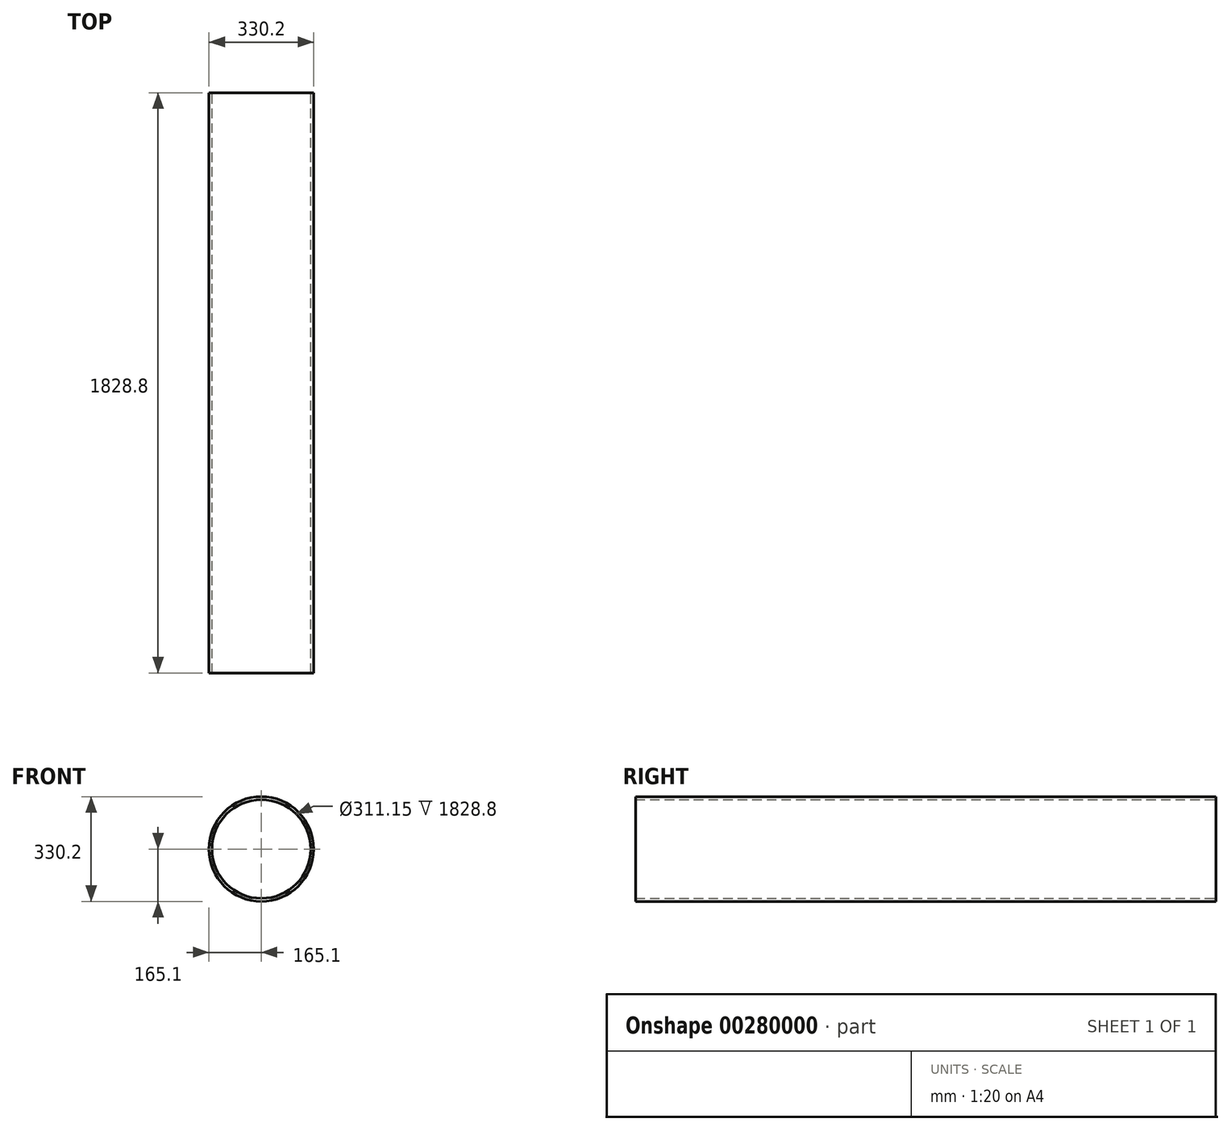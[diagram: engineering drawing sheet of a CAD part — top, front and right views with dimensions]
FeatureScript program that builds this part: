
annotation { "Feature Type Name" : "Feature", "Feature Type Description" : "" }
export const myFeature = defineFeature(function(context is Context, id is Id, definition is map)
    precondition{}
    {
        {
            var Q0;
            Q0=qCreatedBy(makeId("Front.planeOp"),FACE);
            var sketch = newSketch(context, id + "F0", { "sketchPlane" : qUnion([Q0])});
            skCircle(sketch, "E0", {"center": v(0, 0) * mm, "radius": 165.1 * mm});
            skCircle(sketch, "E1", {"center": v(0, 0) * mm, "radius": 155.58 * mm});
            skSolve(sketch);
        }
        {
            var Q0;
            Q0 = qSketchRegion(id + "F0", true);
            var Q1;
            Q1=makeQuery(id+"F0.imprint","IMPRINT",FACE,{"disambiguationData":[TD([[makeQuery(id+"F0.imprint","IMPRINT",EDGE,{"derivedFrom":sQuery(id+"F0.wireOp",EDGE,"E0")}),1.0]])]});
            extrude(context, id + "F1", {"entities" : qUnion([Q0, Q1]), "depth" : 1828.8 * mm});
        }
    });
